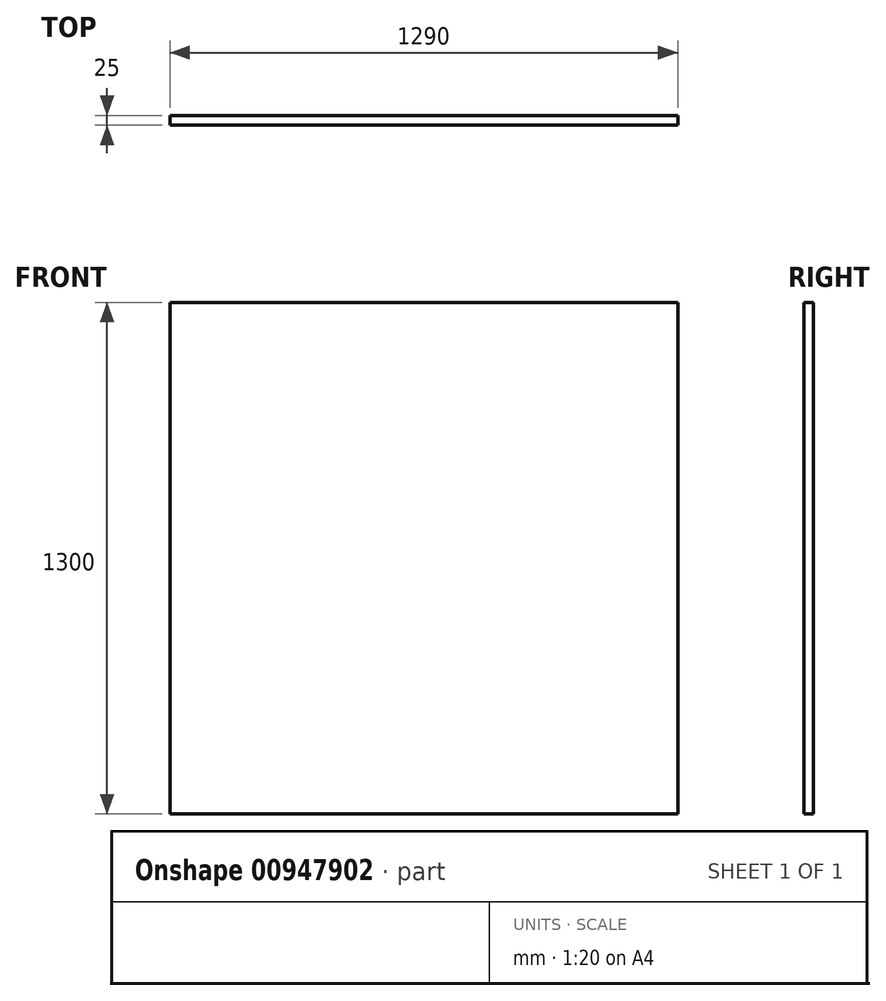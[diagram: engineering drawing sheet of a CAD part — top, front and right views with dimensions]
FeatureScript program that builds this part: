
annotation { "Feature Type Name" : "Feature", "Feature Type Description" : "" }
export const myFeature = defineFeature(function(context is Context, id is Id, definition is map)
    precondition{}
    {
        {
            var Q0;
            Q0=qCreatedBy(makeId("Front.planeOp"),FACE);
            var sketch = newSketch(context, id + "F0", { "sketchPlane" : qUnion([Q0])});
            skLineSegment(sketch, "E0.bottom", {"start": v(-645, 650) * mm, "end": v(645, 650) * mm});
            skLineSegment(sketch, "E0.top", {"start": v(-645, -650) * mm, "end": v(645, -650) * mm});
            skLineSegment(sketch, "E0.left", {"start": v(-645, 650) * mm, "end": v(-645, -650) * mm});
            skLineSegment(sketch, "E0.right", {"start": v(645, 650) * mm, "end": v(645, -650) * mm});
            skPoint(sketch, "E0.middle", {"position": v(0, 0) * mm});
            skSolve(sketch);
        }
        {
            var Q0;
            Q0=makeQuery(id+"F0.imprint","IMPRINT",FACE,{"disambiguationData":[TD([[makeQuery(id+"F0.imprint","IMPRINT",EDGE,{"derivedFrom":sQuery(id+"F0.wireOp",EDGE,"E0.bottom")}),-1.0]])]});
            extrude(context, id + "F1", {"entities" : qUnion([Q0]), "depth" : 25 * mm, "offsetDistance" : 25 * mm});
        }
    });
